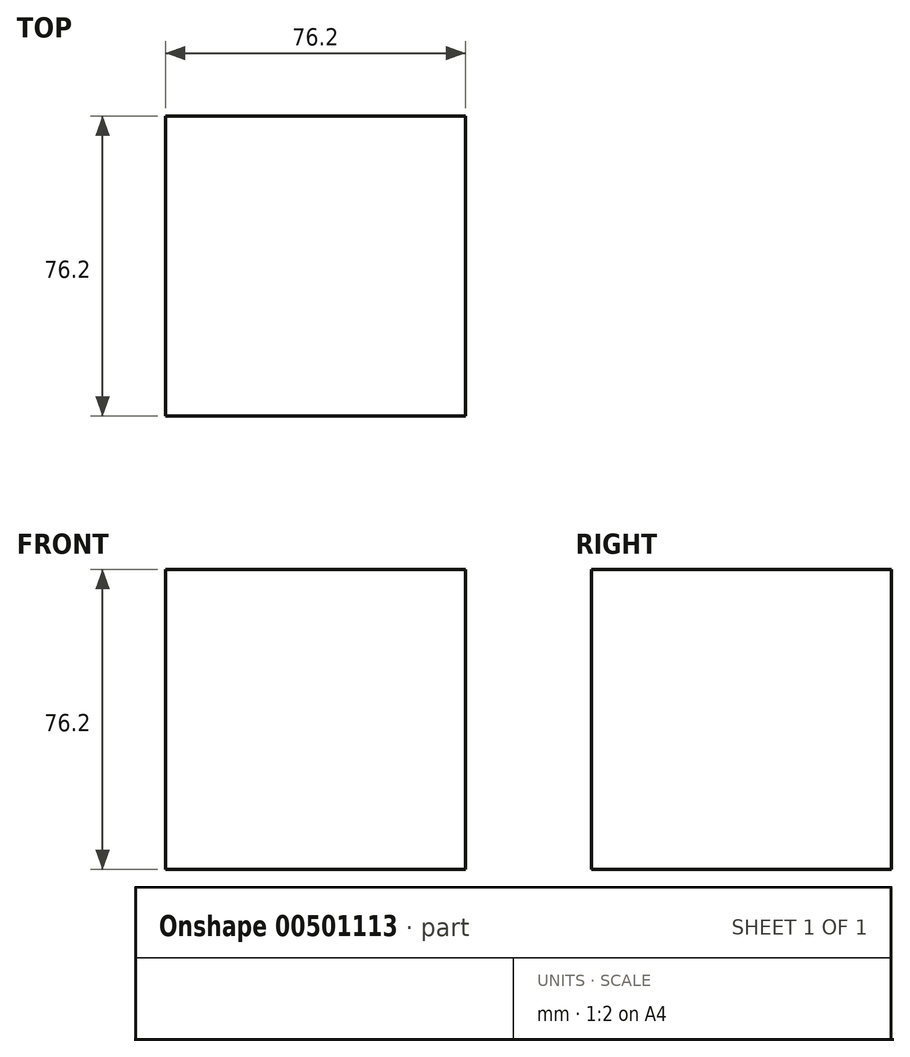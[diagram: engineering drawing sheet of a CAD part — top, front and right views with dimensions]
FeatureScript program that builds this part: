
annotation { "Feature Type Name" : "Feature", "Feature Type Description" : "" }
export const myFeature = defineFeature(function(context is Context, id is Id, definition is map)
    precondition{}
    {
        {
            var Q0;
            Q0=qCreatedBy(makeId("Top.planeOp"),FACE);
            var sketch = newSketch(context, id + "F0", { "sketchPlane" : qUnion([Q0])});
            skLineSegment(sketch, "E0.bottom", {"start": v(-37.87, 38) * mm, "end": v(38.33, 38) * mm});
            skLineSegment(sketch, "E0.top", {"start": v(-37.87, -38.2) * mm, "end": v(38.33, -38.2) * mm});
            skLineSegment(sketch, "E0.left", {"start": v(-37.87, 38) * mm, "end": v(-37.87, -38.2) * mm});
            skLineSegment(sketch, "E0.right", {"start": v(38.33, 38) * mm, "end": v(38.33, -38.2) * mm});
            skSolve(sketch);
        }
        {
            var Q0;
            Q0=makeQuery(id+"F0.imprint","IMPRINT",FACE,{"disambiguationData":[TD([[makeQuery(id+"F0.imprint","IMPRINT",EDGE,{"derivedFrom":sQuery(id+"F0.wireOp",EDGE,"E0.bottom")}),-1.0]])]});
            extrude(context, id + "F1", {"entities" : qUnion([Q0]), "depth" : 76.2 * mm});
        }
    });
